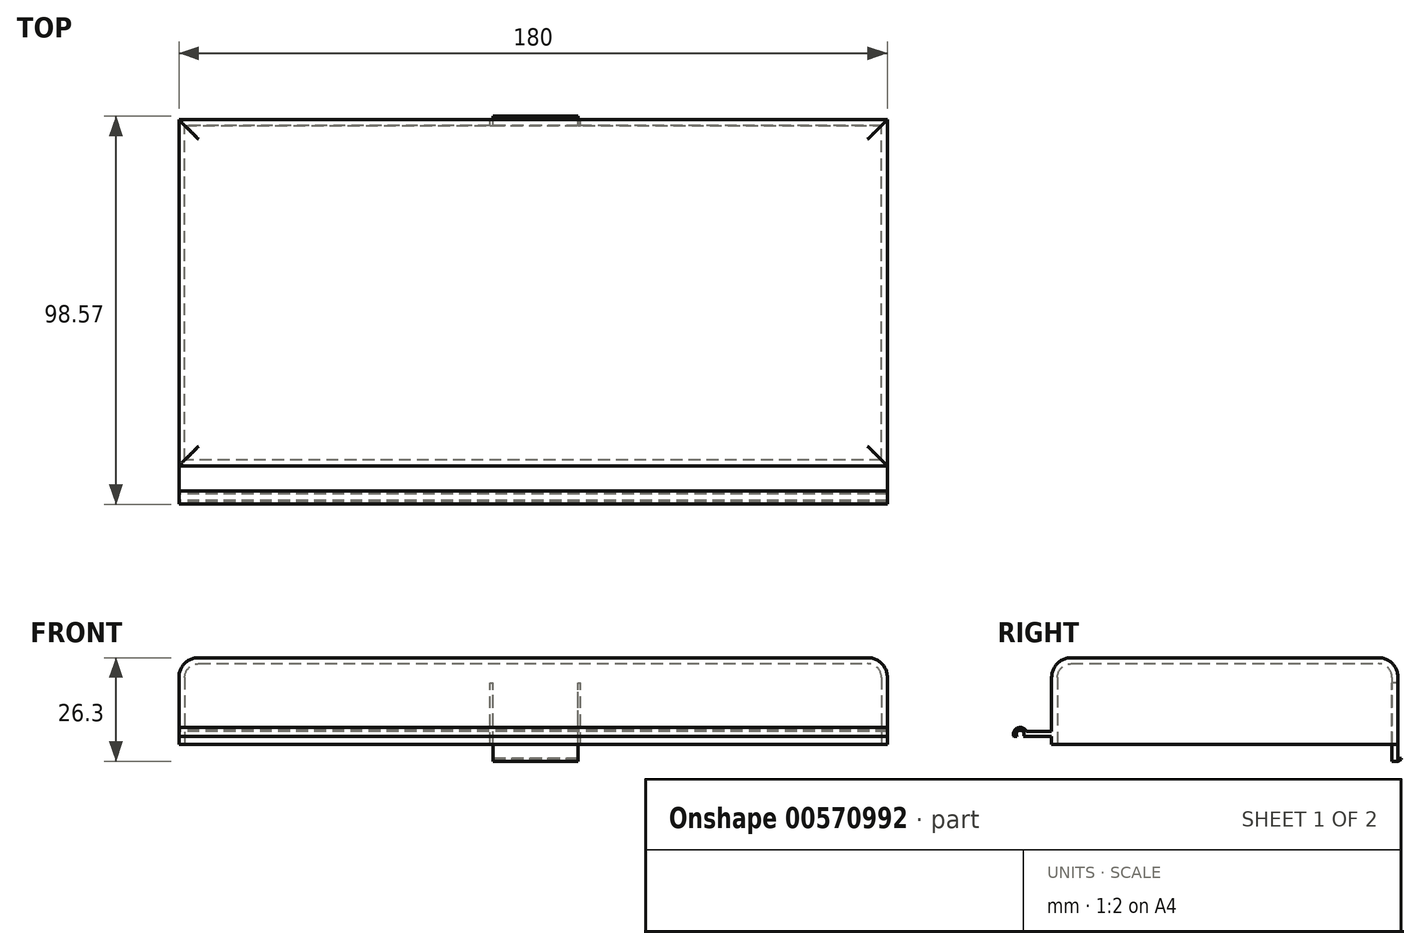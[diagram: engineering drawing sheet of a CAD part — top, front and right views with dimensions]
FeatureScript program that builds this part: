
annotation { "Feature Type Name" : "Feature", "Feature Type Description" : "" }
export const myFeature = defineFeature(function(context is Context, id is Id, definition is map)
    precondition{}
    {
        {
            var Q0;
            Q0=qCreatedBy(makeId("Top.planeOp"),FACE);
            var sketch = newSketch(context, id + "F0", { "sketchPlane" : qUnion([Q0])});
            skLineSegment(sketch, "E0.bottom", {"start": v(90, -44) * mm, "end": v(-90, -44) * mm});
            skLineSegment(sketch, "E0.top", {"start": v(90, 44) * mm, "end": v(-90, 44) * mm});
            skLineSegment(sketch, "E0.left", {"start": v(90, -44) * mm, "end": v(90, 44) * mm});
            skLineSegment(sketch, "E0.right", {"start": v(-90, -44) * mm, "end": v(-90, 44) * mm});
            skPoint(sketch, "E0.middle", {"position": v(0, 0) * mm});
            skSolve(sketch);
        }
        {
            var Q0;
            Q0=makeQuery(id+"F0.imprint","IMPRINT",FACE,{"disambiguationData":[TD([[makeQuery(id+"F0.imprint","IMPRINT",EDGE,{"derivedFrom":sQuery(id+"F0.wireOp",EDGE,"E0.bottom")}),-1.0]])]});
            extrude(context, id + "F1", {"entities" : qUnion([Q0]), "depth" : 20 * mm, "offsetDistance" : 25 * mm, "hasSecondDirection" : true, "secondDirectionOppositeDirection" : true, "secondDirectionDepth" : 2 * mm});
        }
        {
            var Q0;
            Q0=makeQuery(id+"F1.opExtrude","CAP_FACE",FACE,{"disambiguationData":[OSD([sQuery(id+"F0.wireOp",EDGE,"E0.bottom"),sQuery(id+"F0.wireOp",EDGE,"E0.top"),sQuery(id+"F0.wireOp",EDGE,"E0.left"),sQuery(id+"F0.wireOp",EDGE,"E0.right")])],"isStart":false});
            fillet(context, id + "F2", {"entities" : qUnion([Q0]), "radius" : 5 * mm, "tangentPropagation" : true, "allowEdgeOverflow" : false});
        }
        {
            var Q0;
            Q0=makeQuery(id+"F1.opExtrude","CAP_FACE",FACE,{"disambiguationData":[OSD([sQuery(id+"F0.wireOp",EDGE,"E0.bottom"),sQuery(id+"F0.wireOp",EDGE,"E0.top"),sQuery(id+"F0.wireOp",EDGE,"E0.left"),sQuery(id+"F0.wireOp",EDGE,"E0.right")])],"isStart":true});
            shell(context, id + "F3", {"entities" : qUnion([Q0]), "thickness" : 1.5 * mm});
        }
        {
            var Q0;
            Q0=qCreatedBy(makeId("Right.planeOp"),FACE);
            var sketch = newSketch(context, id + "F4", { "sketchPlane" : qUnion([Q0])});
            skLineSegment(sketch, "E1.bottom", {"start": v(-50.63, 1.28) * mm, "end": v(-43.76, 1.28) * mm});
            skLineSegment(sketch, "E1.top", {"start": v(-50.63, 0) * mm, "end": v(-43.76, 0) * mm});
            skLineSegment(sketch, "E1.left", {"start": v(-50.63, 1.28) * mm, "end": v(-50.63, 0) * mm});
            skLineSegment(sketch, "E1.right", {"start": v(-43.76, 1.28) * mm, "end": v(-43.76, 0) * mm});
            skSolve(sketch);
        }
        {
            var Q0;
            Q0 = qSketchRegion(id + "F4", true);
            extrude(context, id + "F5", {"entities" : qUnion([Q0]), "operationType" : NewBodyOperationType.ADD, "depth" : 90 * mm, "offsetDistance" : 25 * mm, "hasSecondDirection" : true, "secondDirectionOppositeDirection" : true, "secondDirectionDepth" : 90 * mm});
        }
        {
            var Q0;
            Q0=qCreatedBy(makeId("Right.planeOp"),FACE);
            var sketch = newSketch(context, id + "F6", { "sketchPlane" : qUnion([Q0])});
            skCircle(sketch, "E2", {"center": v(-51.97, 0.54) * mm, "radius": 1.75 * mm});
            skCircle(sketch, "E3", {"center": v(-51.97, 0.54) * mm, "radius": 1 * mm});
            skSolve(sketch);
        }
        {
            var Q0;
            Q0=makeQuery(id+"F6.imprint","IMPRINT",FACE,{"disambiguationData":[TD([[makeQuery(id+"F6.imprint","IMPRINT",EDGE,{"derivedFrom":sQuery(id+"F6.wireOp",EDGE,"E2")}),1.0]])]});
            extrude(context, id + "F7", {"entities" : qUnion([Q0]), "operationType" : NewBodyOperationType.ADD, "depth" : 90 * mm, "offsetDistance" : 25 * mm, "hasSecondDirection" : true, "secondDirectionOppositeDirection" : true, "secondDirectionDepth" : 90 * mm});
        }
        {
            var Q0;
            Q0=qCreatedBy(makeId("Right.planeOp"),FACE);
            var sketch = newSketch(context, id + "F8", { "sketchPlane" : qUnion([Q0])});
            skLineSegment(sketch, "E4.bottom", {"start": v(-50.28, -1.71) * mm, "end": v(-55.61, -1.71) * mm});
            skLineSegment(sketch, "E4.top", {"start": v(-50.28, 0) * mm, "end": v(-55.61, 0) * mm});
            skLineSegment(sketch, "E4.left", {"start": v(-50.28, -1.71) * mm, "end": v(-50.28, 0) * mm});
            skLineSegment(sketch, "E4.right", {"start": v(-55.61, -1.71) * mm, "end": v(-55.61, 0) * mm});
            skSolve(sketch);
        }
        {
            var Q0;
            Q0=makeQuery(id+"F8.imprint","IMPRINT",FACE,{"disambiguationData":[TD([[makeQuery(id+"F8.imprint","IMPRINT",EDGE,{"derivedFrom":sQuery(id+"F8.wireOp",EDGE,"E4.bottom")}),-1.0]])]});
            extrude(context, id + "F9", {"entities" : qUnion([Q0]), "operationType" : NewBodyOperationType.REMOVE, "depth" : 90 * mm, "offsetDistance" : 25 * mm, "hasSecondDirection" : true, "secondDirectionOppositeDirection" : true, "secondDirectionDepth" : 90 * mm});
        }
        {
            var Q0;
            Q0=makeQuery(id+"F8.imprint","IMPRINT",FACE,{"disambiguationData":[TD([[makeQuery(id+"F8.imprint","IMPRINT",EDGE,{"derivedFrom":sQuery(id+"F8.wireOp",EDGE,"E4.bottom")}),-1.0]])]});
            extrude(context, id + "F10", {"entities" : qUnion([Q0]), "operationType" : NewBodyOperationType.REMOVE, "oppositeDirection" : true, "depth" : 80 * mm, "offsetDistance" : 25 * mm, "hasSecondDirection" : true, "secondDirectionOppositeDirection" : false, "secondDirectionDepth" : 80 * mm});
        }
        {
            var Q0;
            Q0=qCreatedBy(makeId("Front.planeOp"),FACE);
            var sketch = newSketch(context, id + "F11", { "sketchPlane" : qUnion([Q0])});
            skLineSegment(sketch, "E5.bottom", {"start": v(11.42, -3.73) * mm, "end": v(12.08, -3.73) * mm});
            skLineSegment(sketch, "E5.top", {"start": v(11.42, 13.62) * mm, "end": v(12.08, 13.62) * mm});
            skLineSegment(sketch, "E5.left", {"start": v(11.42, -3.73) * mm, "end": v(11.42, 13.62) * mm});
            skLineSegment(sketch, "E5.right", {"start": v(12.08, -3.73) * mm, "end": v(12.08, 13.62) * mm});
            skLineSegment(sketch, "E6.bottom", {"start": v(-10.94, -3.8) * mm, "end": v(-10.21, -3.8) * mm});
            skLineSegment(sketch, "E6.top", {"start": v(-10.94, 13.62) * mm, "end": v(-10.21, 13.62) * mm});
            skLineSegment(sketch, "E6.left", {"start": v(-10.94, -3.8) * mm, "end": v(-10.94, 13.62) * mm});
            skLineSegment(sketch, "E6.right", {"start": v(-10.21, -3.8) * mm, "end": v(-10.21, 13.62) * mm});
            skSolve(sketch);
        }
        {
            var Q0;
            Q0 = qSketchRegion(id + "F11", true);
            extrude(context, id + "F12", {"entities" : qUnion([Q0]), "operationType" : NewBodyOperationType.REMOVE, "oppositeDirection" : true, "depth" : 55.1 * mm, "offsetDistance" : 25 * mm});
        }
        {
            var Q0;
            {var subQ0=sQuery(id+"F0.wireOp",EDGE,"E0.top");Q0=makeQuery(id+"F12.boolean.opBoolean","SPLIT",FACE,{"disambiguationData":[TD([makeQuery(id+"F12.opExtrude","SWEPT_FACE",FACE,{"disambiguationData":[OSD([sQuery(id+"F11.wireOp",EDGE,"E5.left")])]})])],"derivedFrom":makeQuery(id+"F1.opExtrude","CAP_FACE",FACE,{"disambiguationData":[OSD([sQuery(id+"F0.wireOp",EDGE,"E0.bottom"),subQ0,sQuery(id+"F0.wireOp",EDGE,"E0.left"),sQuery(id+"F0.wireOp",EDGE,"E0.right")])],"isStart":true})});}
            extrude(context, id + "F13", {"entities" : qUnion([Q0]), "operationType" : NewBodyOperationType.ADD, "depth" : 4.3 * mm, "offsetDistance" : 25 * mm});
        }
        {
            var Q0;
            Q0=qCreatedBy(makeId("Right.planeOp"),FACE);
            var sketch = newSketch(context, id + "F14", { "sketchPlane" : qUnion([Q0])});
            skLineSegment(sketch, "E7", {"start": v(44, -6.3) * mm, "end": v(44.85, -5.86) * mm});
            skLineSegment(sketch, "E8", {"start": v(44.85, -5.86) * mm, "end": v(44.85, -5.53) * mm});
            skLineSegment(sketch, "E9", {"start": v(44.85, -5.53) * mm, "end": v(43.99, -5.53) * mm});
            skLineSegment(sketch, "E10", {"start": v(43.99, -5.53) * mm, "end": v(43.99, -6.3) * mm});
            skLineSegment(sketch, "E11", {"start": v(43.99, -6.3) * mm, "end": v(44, -6.3) * mm});
            skSolve(sketch);
        }
        {
            var Q0;
            Q0=makeQuery(id+"F14.imprint","IMPRINT",FACE,{"disambiguationData":[TD([[makeQuery(id+"F14.imprint","IMPRINT",EDGE,{"derivedFrom":sQuery(id+"F14.wireOp",EDGE,"E7")}),1.0]])]});
            extrude(context, id + "F15", {"entities" : qUnion([Q0]), "operationType" : NewBodyOperationType.ADD, "depth" : 11.43 * mm, "offsetDistance" : 25 * mm, "hasSecondDirection" : true, "secondDirectionOppositeDirection" : true, "secondDirectionDepth" : 10.21 * mm});
        }
    });
